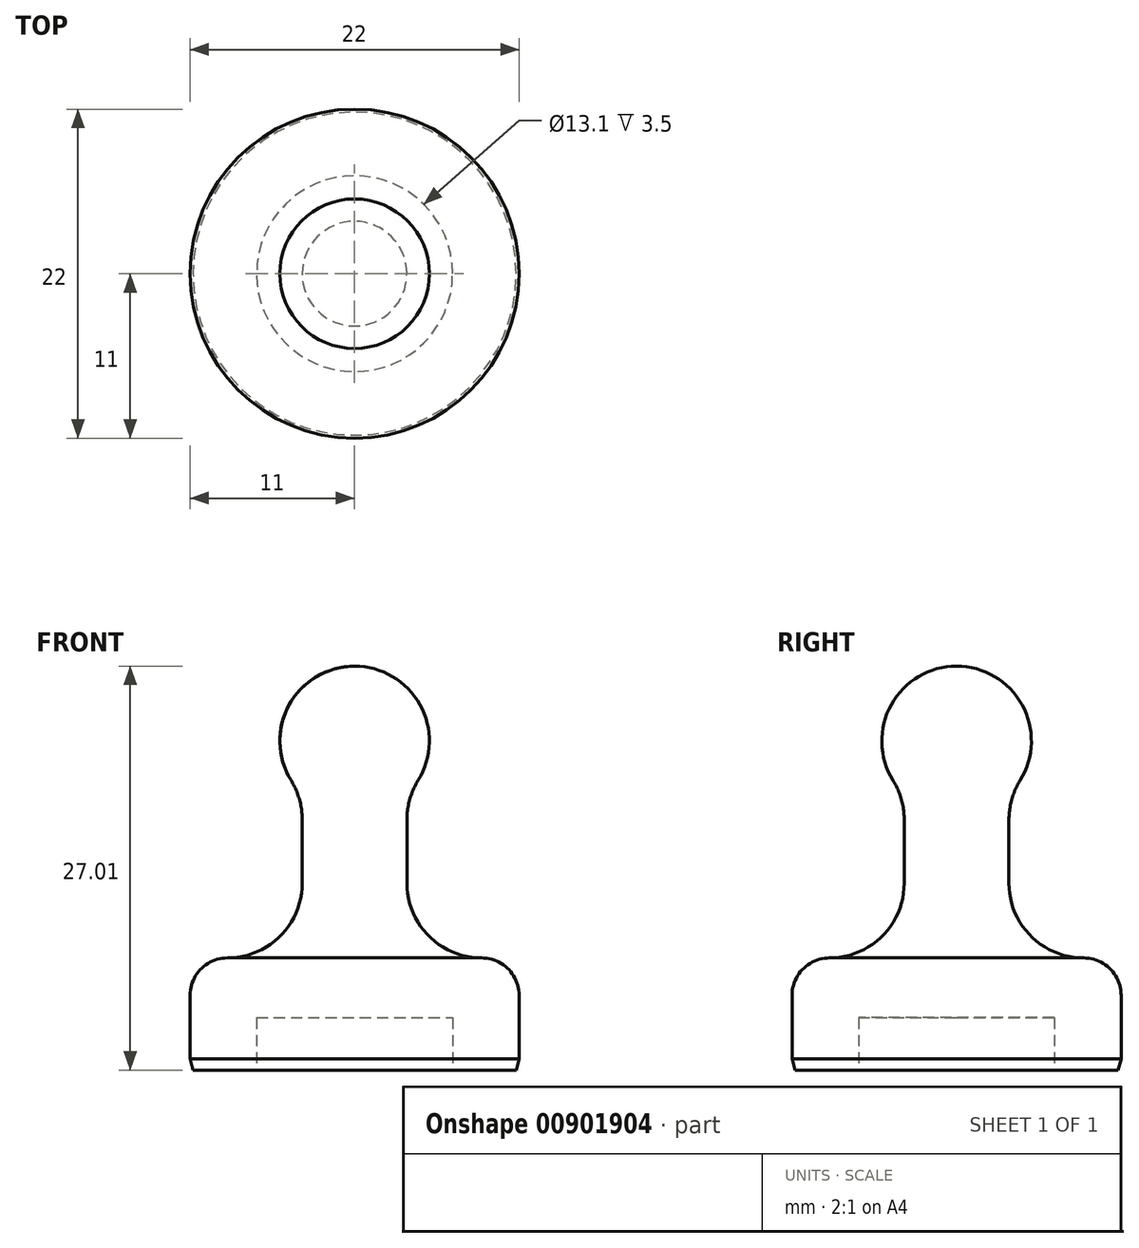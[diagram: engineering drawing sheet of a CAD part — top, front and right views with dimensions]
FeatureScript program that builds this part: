
annotation { "Feature Type Name" : "Feature", "Feature Type Description" : "" }
export const myFeature = defineFeature(function(context is Context, id is Id, definition is map)
    precondition{}
    {
        {
            var Q0;
            Q0=qCreatedBy(makeId("Front.planeOp"),FACE);
            var sketch = newSketch(context, id + "F0", { "sketchPlane" : qUnion([Q0])});
            skLineSegment(sketch, "E0", {"start": v(1, 3.5) * mm, "end": v(1, 27.01) * mm});
            skLineSegment(sketch, "E1", {"start": v(-5.55, 0) * mm, "end": v(-9.8, 0) * mm});
            skLineSegment(sketch, "E2", {"start": v(-10, 0.74) * mm, "end": v(-10, 5) * mm});
            skArc(sketch, "E3", {"start": v(1, 27.01) * mm, "mid": v(-3.37, 24.44) * mm, "end": v(-3.25, 19.38) * mm});
            skLineSegment(sketch, "E4", {"start": v(-2.5, 16.74) * mm, "end": v(-2.5, 12.5) * mm});
            skLineSegment(sketch, "E5", {"start": v(-7.5, 7.5) * mm, "end": v(-7.5, 7.5) * mm});
            skPoint(sketch, "E6.visualSharp", {"position": v(-2.5, 18.44) * mm});
            skArc(sketch, "E6.filletArc", {"start": v(-2.5, 16.74) * mm, "mid": v(-2.7, 18.11) * mm, "end": v(-3.25, 19.38) * mm});
            skPoint(sketch, "E7.visualSharp", {"position": v(-2.5, 7.5) * mm});
            skArc(sketch, "E7.filletArc", {"start": v(-7.5, 7.5) * mm, "mid": v(-3.96, 8.96) * mm, "end": v(-2.5, 12.5) * mm});
            skPoint(sketch, "E8.visualSharp", {"position": v(-10, 7.5) * mm});
            skArc(sketch, "E8.filletArc", {"start": v(-7.5, 7.5) * mm, "mid": v(-9.27, 6.77) * mm, "end": v(-10, 5) * mm});
            skLineSegment(sketch, "E9", {"start": v(1, 3.5) * mm, "end": v(-5.55, 3.5) * mm});
            skLineSegment(sketch, "E10", {"start": v(-5.55, 3.5) * mm, "end": v(-5.55, 0) * mm});
            skLineSegment(sketch, "E11", {"start": v(-9.8, 0) * mm, "end": v(-10, 0.74) * mm});
            skPoint(sketch, "E12.orphan", {"position": v(-10, 0) * mm});
            skSolve(sketch);
        }
        {
            var Q0;
            Q0=makeQuery(id+"F0.imprint","IMPRINT",FACE,{"disambiguationData":[TD([[makeQuery(id+"F0.imprint","IMPRINT",EDGE,{"derivedFrom":sQuery(id+"F0.wireOp",EDGE,"E0")}),1.0]])]});
            var Q1;
            Q1=sQuery(id+"F0.wireOp",EDGE,"E0");
            revolve(context, id + "F1", {"surfaceOperationType" : NewSurfaceOperationType.NEW, "entities" : qUnion([Q0]), "axis" : qUnion([Q1]), "revolveType" : RevolveType.FULL});
        }
    });
